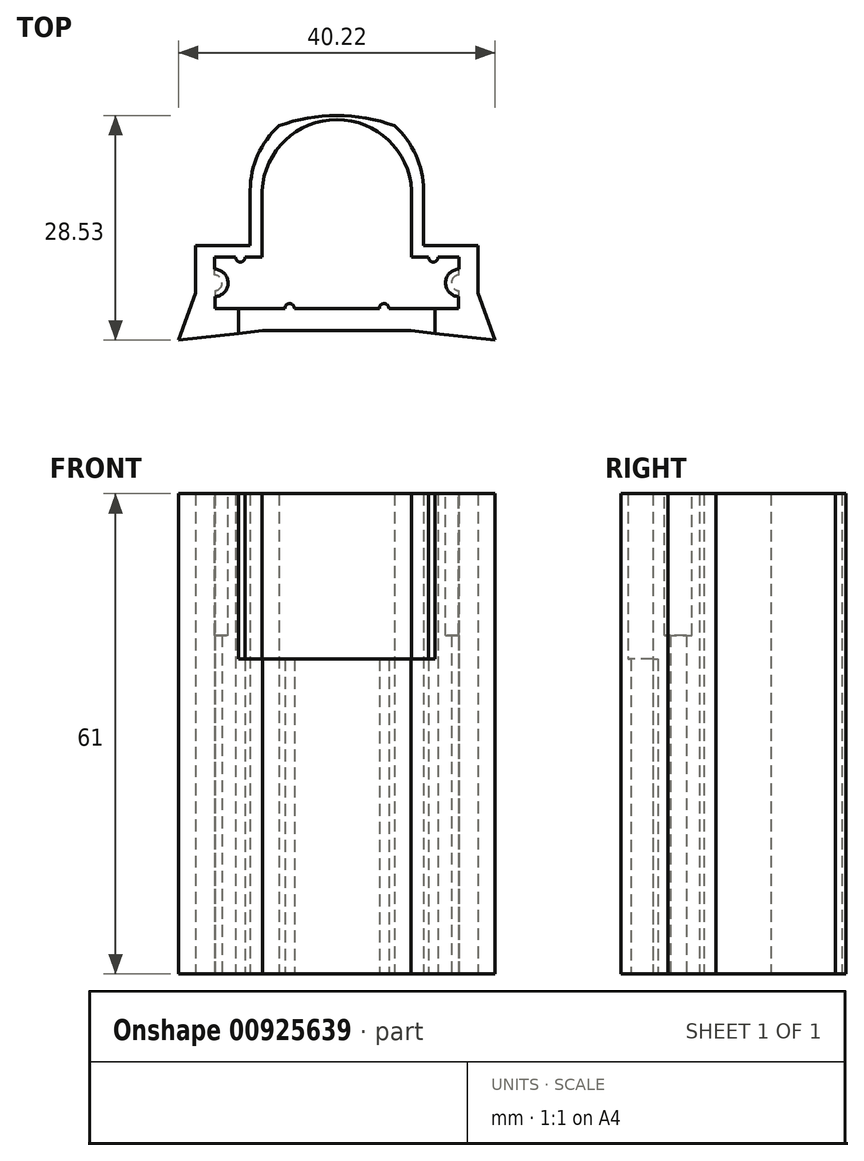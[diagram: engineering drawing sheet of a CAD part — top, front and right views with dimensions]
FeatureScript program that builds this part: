
annotation { "Feature Type Name" : "Feature", "Feature Type Description" : "" }
export const myFeature = defineFeature(function(context is Context, id is Id, definition is map)
    precondition{}
    {
        {
            var Q0;
            Q0=qCreatedBy(makeId("Top.planeOp"),FACE);
            var sketch = newSketch(context, id + "F0", { "sketchPlane" : qUnion([Q0])});
            skLineSegment(sketch, "E0", {"start": v(-9.5, 8.35) * mm, "end": v(-9.5, -0.15) * mm});
            skArc(sketch, "E1", {"start": v(-12.86, -0.15) * mm, "mid": v(-12.26, -0.75) * mm, "end": v(-11.66, -0.15) * mm});
            skArc(sketch, "E2", {"start": v(-15.48, -4.4) * mm, "mid": v(-14.57, -3.39) * mm, "end": v(-15.5, -2.4) * mm});
            skArc(sketch, "E3", {"start": v(-5.4, -6.65) * mm, "mid": v(-6, -6.03) * mm, "end": v(-6.6, -6.65) * mm});
            skLineSegment(sketch, "E4", {"start": v(-11.66, -0.15) * mm, "end": v(-9.5, -0.15) * mm});
            skLineSegment(sketch, "E5", {"start": v(-12.86, -0.15) * mm, "end": v(-15.5, -0.15) * mm});
            skLineSegment(sketch, "E6", {"start": v(-15.5, -2.4) * mm, "end": v(-15.5, -0.15) * mm});
            skLineSegment(sketch, "E7", {"start": v(-15.48, -4.4) * mm, "end": v(-15.48, -6.65) * mm});
            skLineSegment(sketch, "E8", {"start": v(-15.48, -6.65) * mm, "end": v(-6.6, -6.65) * mm});
            skLineSegment(sketch, "E9", {"start": v(-5.4, -6.65) * mm, "end": v(0, -6.65) * mm});
            skLineSegment(sketch, "E10", {"start": v(0, -6.65) * mm, "end": v(0, -9.46) * mm});
            skLineSegment(sketch, "E11", {"start": v(-17.92, 1.35) * mm, "end": v(-11, 1.35) * mm});
            skLineSegment(sketch, "E12", {"start": v(-11, 1.35) * mm, "end": v(-11, 8.35) * mm});
            skLineSegment(sketch, "E13", {"start": v(-17.92, -4.7) * mm, "end": v(-20.1, -10.68) * mm});
            skLineSegment(sketch, "E14", {"start": v(-20.1, -10.68) * mm, "end": v(-9.42, -9.46) * mm});
            skLineSegment(sketch, "E15", {"start": v(-17.92, -4.7) * mm, "end": v(-17.92, 1.35) * mm});
            skLineSegment(sketch, "E16", {"start": v(-9.42, -9.46) * mm, "end": v(0, -9.46) * mm});
            skLineSegment(sketch, "E17.MirrorCS", {"start": v(9.5, 8.35) * mm, "end": v(9.5, -0.15) * mm});
            skLineSegment(sketch, "E18.MirrorCS", {"start": v(11, 1.35) * mm, "end": v(11, 8.35) * mm});
            skLineSegment(sketch, "E19.MirrorCS", {"start": v(17.92, 1.35) * mm, "end": v(11, 1.35) * mm});
            skLineSegment(sketch, "E20.MirrorCS", {"start": v(11.66, -0.15) * mm, "end": v(9.5, -0.15) * mm});
            skArc(sketch, "E21.MirrorCS", {"start": v(12.86, -0.15) * mm, "mid": v(12.26, -0.75) * mm, "end": v(11.66, -0.15) * mm});
            skLineSegment(sketch, "E22.MirrorCS", {"start": v(12.86, -0.15) * mm, "end": v(15.5, -0.15) * mm});
            skLineSegment(sketch, "E23.MirrorCS", {"start": v(17.92, -4.7) * mm, "end": v(17.92, 1.35) * mm});
            skLineSegment(sketch, "E24.MirrorCS", {"start": v(17.92, -4.7) * mm, "end": v(20.1, -10.68) * mm});
            skLineSegment(sketch, "E25.MirrorCS", {"start": v(15.48, -4.4) * mm, "end": v(15.48, -6.65) * mm});
            skArc(sketch, "E26.MirrorCS", {"start": v(15.48, -4.4) * mm, "mid": v(14.57, -3.39) * mm, "end": v(15.5, -2.4) * mm});
            skLineSegment(sketch, "E27.MirrorCS", {"start": v(15.5, -2.4) * mm, "end": v(15.5, -0.15) * mm});
            skLineSegment(sketch, "E28.MirrorCS", {"start": v(15.48, -6.65) * mm, "end": v(6.6, -6.65) * mm});
            skArc(sketch, "E29.MirrorCS", {"start": v(5.4, -6.65) * mm, "mid": v(6, -6.03) * mm, "end": v(6.6, -6.65) * mm});
            skLineSegment(sketch, "E30.MirrorCS", {"start": v(5.4, -6.65) * mm, "end": v(0, -6.65) * mm});
            skLineSegment(sketch, "E31.MirrorCS", {"start": v(9.42, -9.46) * mm, "end": v(0, -9.46) * mm});
            skLineSegment(sketch, "E32.MirrorCS", {"start": v(20.1, -10.68) * mm, "end": v(9.42, -9.46) * mm});
            skArc(sketch, "E33", {"start": v(-11, 8.35) * mm, "mid": v(-10.04, 12.84) * mm, "end": v(-7.33, 16.55) * mm});
            skArc(sketch, "E34", {"start": v(11, 8.35) * mm, "mid": v(10.04, 12.84) * mm, "end": v(7.33, 16.55) * mm});
            skArc(sketch, "E35", {"start": v(-7.33, 16.55) * mm, "mid": v(0, 17.85) * mm, "end": v(7.33, 16.55) * mm});
            skLineSegment(sketch, "E36", {"start": v(0, 17.85) * mm, "end": v(0, 17.35) * mm});
            skArc(sketch, "E37", {"start": v(9.5, 8.35) * mm, "mid": v(0, 17.35) * mm, "end": v(-9.5, 8.35) * mm});
            skSolve(sketch);
        }
        {
            var Q0;
            Q0=makeQuery(id+"F0.imprint","IMPRINT",FACE,{"disambiguationData":[TD([[makeQuery(id+"F0.imprint","IMPRINT",EDGE,{"derivedFrom":sQuery(id+"F0.wireOp",EDGE,"E0")}),-1.0]])]});
            var Q1;
            Q1=makeQuery(id+"F0.imprint","IMPRINT",FACE,{"disambiguationData":[TD([[makeQuery(id+"F0.imprint","IMPRINT",EDGE,{"derivedFrom":sQuery(id+"F0.wireOp",EDGE,"E10")}),1.0]])]});
            extrude(context, id + "F1", {"entities" : qUnion([Q0, Q1]), "depth" : 61 * mm, "offsetDistance" : 25 * mm});
        }
        {
            var Q0;
            Q0=makeQuery(id+"F1.opExtrude","SWEPT_FACE",FACE,{"disambiguationData":[OSD([sQuery(id+"F0.wireOp",EDGE,"E16"),sQuery(id+"F0.wireOp",EDGE,"E31.MirrorCS")])]});
            var sketch = newSketch(context, id + "F2", { "sketchPlane" : qUnion([Q0])});
            skLineSegment(sketch, "E38.bottom", {"start": v(12.5, 61) * mm, "end": v(-12.5, 61) * mm});
            skLineSegment(sketch, "E38.top", {"start": v(12.5, 40) * mm, "end": v(-12.5, 40) * mm});
            skLineSegment(sketch, "E38.left", {"start": v(12.5, 61) * mm, "end": v(12.5, 40) * mm});
            skLineSegment(sketch, "E38.right", {"start": v(-12.5, 61) * mm, "end": v(-12.5, 40) * mm});
            skSolve(sketch);
        }
        {
            var Q0;
            Q0 = qSketchRegion(id + "F2", true);
            extrude(context, id + "F3", {"entities" : qUnion([Q0]), "operationType" : NewBodyOperationType.REMOVE, "endBound" : BoundingType.SYMMETRIC, "oppositeDirection" : true, "depth" : 8 * mm, "offsetDistance" : 25 * mm});
        }
        {
            var Q0;
            Q0=makeQuery(id+"F1.opExtrude","CAP_FACE",FACE,{"disambiguationData":[OSD([sQuery(id+"F0.wireOp",EDGE,"E0"),sQuery(id+"F0.wireOp",EDGE,"E1"),sQuery(id+"F0.wireOp",EDGE,"E2"),sQuery(id+"F0.wireOp",EDGE,"E3"),sQuery(id+"F0.wireOp",EDGE,"E4"),sQuery(id+"F0.wireOp",EDGE,"E5"),sQuery(id+"F0.wireOp",EDGE,"E6"),sQuery(id+"F0.wireOp",EDGE,"E7"),sQuery(id+"F0.wireOp",EDGE,"E8"),sQuery(id+"F0.wireOp",EDGE,"E9"),sQuery(id+"F0.wireOp",EDGE,"E11"),sQuery(id+"F0.wireOp",EDGE,"E12"),sQuery(id+"F0.wireOp",EDGE,"SOZslnYQ-E4Is-6qd0-o9PI-dPW1uWQMbFkM"),sQuery(id+"F0.wireOp",EDGE,"5kG84hzZ-tjHW-8SOO-e1Oj-BtrOo1oCBrCn"),sQuery(id+"F0.wireOp",EDGE,"E13"),sQuery(id+"F0.wireOp",EDGE,"E14"),sQuery(id+"F0.wireOp",EDGE,"E15"),sQuery(id+"F0.wireOp",EDGE,"E16"),sQuery(id+"F0.wireOp",EDGE,"FWTEwcpr-XYvV-oLHS-gAoL-tD9ZZ0mwxul8"),sQuery(id+"F0.wireOp",EDGE,"abe5c25b-6797-4b88-8245-2bb95bd30bf20.MirrorCS"),sQuery(id+"F0.wireOp",EDGE,"6afb71d5-8208-48a5-896e-f1c779d42a890.MirrorCS"),sQuery(id+"F0.wireOp",EDGE,"d8a0921e-d8e1-42a6-8953-701130f043ce0.MirrorCS"),sQuery(id+"F0.wireOp",EDGE,"E17.MirrorCS"),sQuery(id+"F0.wireOp",EDGE,"E18.MirrorCS"),sQuery(id+"F0.wireOp",EDGE,"E19.MirrorCS"),sQuery(id+"F0.wireOp",EDGE,"E20.MirrorCS"),sQuery(id+"F0.wireOp",EDGE,"E21.MirrorCS"),sQuery(id+"F0.wireOp",EDGE,"E22.MirrorCS"),sQuery(id+"F0.wireOp",EDGE,"E23.MirrorCS"),sQuery(id+"F0.wireOp",EDGE,"E24.MirrorCS"),sQuery(id+"F0.wireOp",EDGE,"E25.MirrorCS"),sQuery(id+"F0.wireOp",EDGE,"E26.MirrorCS"),sQuery(id+"F0.wireOp",EDGE,"E27.MirrorCS"),sQuery(id+"F0.wireOp",EDGE,"E28.MirrorCS"),sQuery(id+"F0.wireOp",EDGE,"E29.MirrorCS"),sQuery(id+"F0.wireOp",EDGE,"E30.MirrorCS"),sQuery(id+"F0.wireOp",EDGE,"E31.MirrorCS"),sQuery(id+"F0.wireOp",EDGE,"E32.MirrorCS")])],"isStart":false});
            var sketch = newSketch(context, id + "F4", { "sketchPlane" : qUnion([Q0])});
            skCircle(sketch, "E39", {"center": v(-15.57, -3.4) * mm, "radius": 1.75 * mm});
            skCircle(sketch, "E40", {"center": v(15.57, -3.4) * mm, "radius": 1.75 * mm});
            skSolve(sketch);
        }
        {
            var Q0;
            Q0 = qSketchRegion(id + "F4", true);
            extrude(context, id + "F5", {"entities" : qUnion([Q0]), "operationType" : NewBodyOperationType.ADD, "oppositeDirection" : true, "depth" : 18 * mm, "offsetDistance" : 25 * mm});
        }
    });
